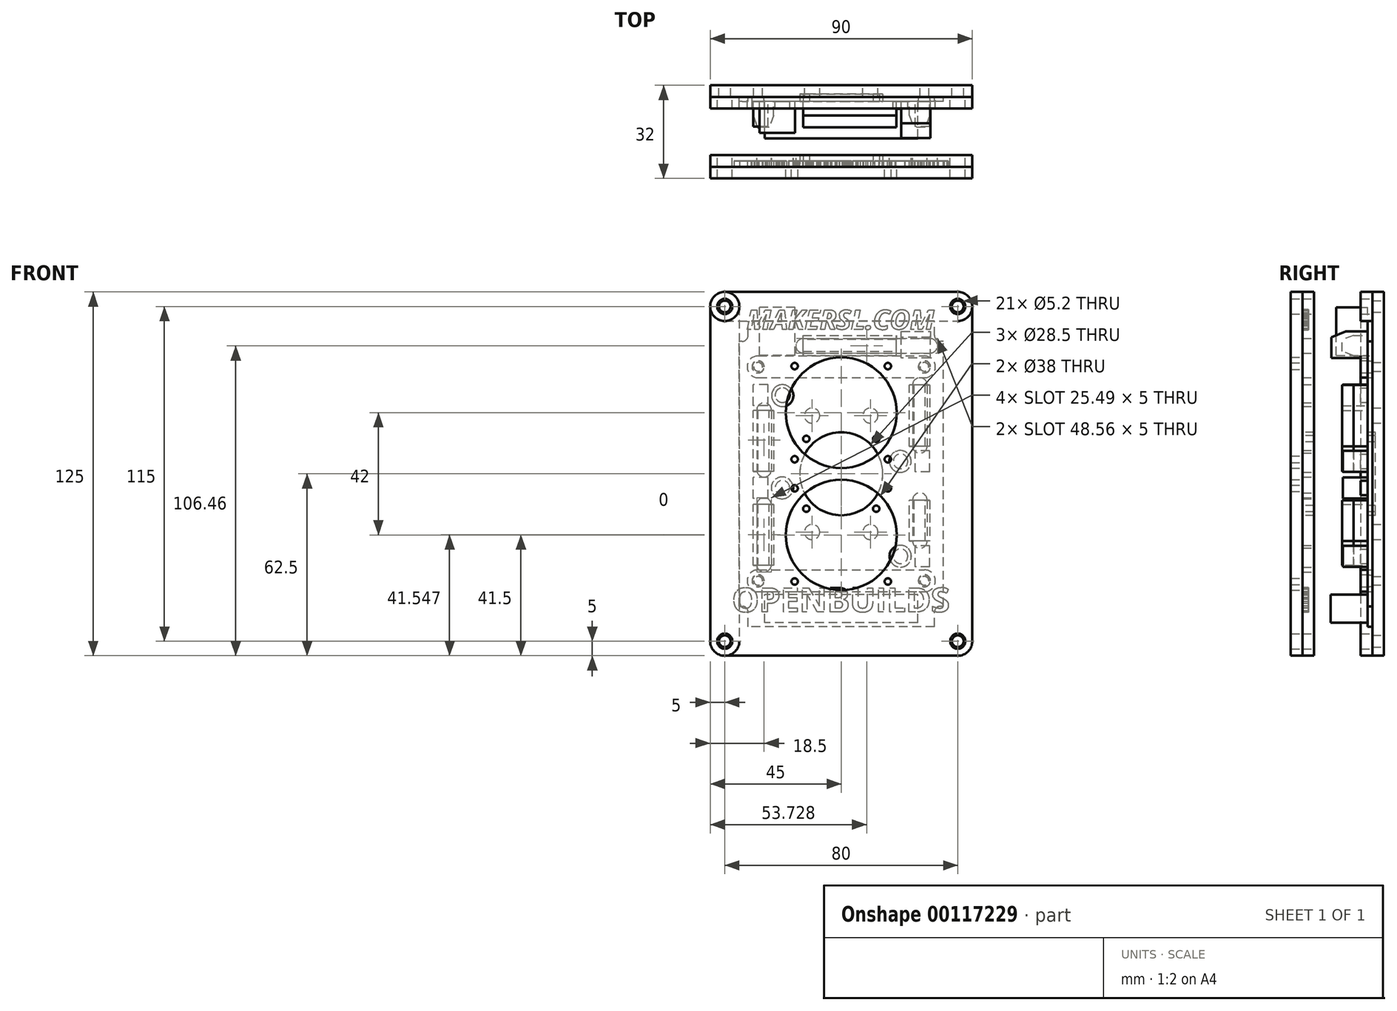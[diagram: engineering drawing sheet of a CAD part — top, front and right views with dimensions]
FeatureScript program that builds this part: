
annotation { "Feature Type Name" : "Feature", "Feature Type Description" : "" }
export const myFeature = defineFeature(function(context is Context, id is Id, definition is map)
    precondition{}
    {
        {
            var Q0;
            Q0=qCreatedBy(makeId("Front.planeOp"),FACE);
            var sketch = newSketch(context, id + "F0", { "sketchPlane" : qUnion([Q0])});
            skPoint(sketch, "E0.middle", {"position": v(0, 0) * mm});
            skLineSegment(sketch, "E1.bottom", {"start": v(10, -20) * mm, "end": v(-10, -20) * mm, "construction": true});
            skLineSegment(sketch, "E1.top", {"start": v(10, 20) * mm, "end": v(-10, 20) * mm, "construction": true});
            skLineSegment(sketch, "E1.left", {"start": v(10, -20) * mm, "end": v(10, 20) * mm, "construction": true});
            skLineSegment(sketch, "E1.right", {"start": v(-10, -20) * mm, "end": v(-10, 20) * mm, "construction": true});
            skCircle(sketch, "E2", {"center": v(-10, 20) * mm, "radius": 2.6 * mm});
            skCircle(sketch, "E3", {"center": v(10, 20) * mm, "radius": 2.6 * mm});
            skCircle(sketch, "E4", {"center": v(10, -20) * mm, "radius": 2.6 * mm});
            skCircle(sketch, "E5", {"center": v(-10, -20) * mm, "radius": 2.6 * mm});
            skLineSegment(sketch, "E6.bottom", {"start": v(28.55, -36.75) * mm, "end": v(-28.55, -36.75) * mm, "construction": true});
            skLineSegment(sketch, "E6.top", {"start": v(28.55, 36.75) * mm, "end": v(-28.55, 36.75) * mm, "construction": true});
            skLineSegment(sketch, "E6.left", {"start": v(28.55, -36.75) * mm, "end": v(28.55, 36.75) * mm, "construction": true});
            skLineSegment(sketch, "E6.right", {"start": v(-28.55, -36.75) * mm, "end": v(-28.55, 36.75) * mm, "construction": true});
            skCircle(sketch, "E7", {"center": v(-28.55, 36.75) * mm, "radius": 1.5 * mm});
            skCircle(sketch, "E8", {"center": v(28.55, 36.75) * mm, "radius": 1.5 * mm});
            skCircle(sketch, "E9", {"center": v(28.55, -36.75) * mm, "radius": 1.5 * mm});
            skCircle(sketch, "E10", {"center": v(-28.55, -36.75) * mm, "radius": 1.5 * mm});
            skLineSegment(sketch, "E11.bottom", {"start": v(40, -62.5) * mm, "end": v(-40, -62.5) * mm});
            skLineSegment(sketch, "E11.top", {"start": v(40, 62.5) * mm, "end": v(-40, 62.5) * mm});
            skLineSegment(sketch, "E11.left", {"start": v(45, -57.5) * mm, "end": v(45, 57.5) * mm});
            skLineSegment(sketch, "E11.right", {"start": v(-45, -57.5) * mm, "end": v(-45, 57.5) * mm});
            skPoint(sketch, "E12.visualSharp", {"position": v(-45, 62.5) * mm});
            skArc(sketch, "E12.filletArc", {"start": v(-40, 62.5) * mm, "mid": v(-43.54, 61.04) * mm, "end": v(-45, 57.5) * mm});
            skPoint(sketch, "E13.visualSharp", {"position": v(45, 62.5) * mm});
            skArc(sketch, "E13.filletArc", {"start": v(45, 57.5) * mm, "mid": v(43.54, 61.04) * mm, "end": v(40, 62.5) * mm});
            skPoint(sketch, "E14.visualSharp", {"position": v(45, -62.5) * mm});
            skArc(sketch, "E14.filletArc", {"start": v(40, -62.5) * mm, "mid": v(43.54, -61.04) * mm, "end": v(45, -57.5) * mm});
            skPoint(sketch, "E15.visualSharp", {"position": v(-45, -62.5) * mm});
            skArc(sketch, "E15.filletArc", {"start": v(-45, -57.5) * mm, "mid": v(-43.54, -61.04) * mm, "end": v(-40, -62.5) * mm});
            skCircle(sketch, "E16", {"center": v(-40, 57.5) * mm, "radius": 2 * mm});
            skCircle(sketch, "E17", {"center": v(40, 57.5) * mm, "radius": 2 * mm});
            skCircle(sketch, "E18", {"center": v(-40, -57.5) * mm, "radius": 2 * mm});
            skCircle(sketch, "E19", {"center": v(40, -57.5) * mm, "radius": 2 * mm});
            skSolve(sketch);
        }
        {
            var Q0;
            Q0 = qSketchRegion(id + "F0", true);
            extrude(context, id + "F1", {"entities" : qUnion([Q0]), "depth" : 4 * mm});
        }
        {
            var Q0;
            Q0=makeQuery(id+"F1.opExtrude","CAP_FACE",FACE,{"disambiguationData":[OSD([sQuery(id+"F0.wireOp",EDGE,"E2"),sQuery(id+"F0.wireOp",EDGE,"E3"),sQuery(id+"F0.wireOp",EDGE,"E4"),sQuery(id+"F0.wireOp",EDGE,"E5"),sQuery(id+"F0.wireOp",EDGE,"E7"),sQuery(id+"F0.wireOp",EDGE,"E8"),sQuery(id+"F0.wireOp",EDGE,"E9"),sQuery(id+"F0.wireOp",EDGE,"E10"),sQuery(id+"F0.wireOp",EDGE,"E11.bottom"),sQuery(id+"F0.wireOp",EDGE,"E11.top"),sQuery(id+"F0.wireOp",EDGE,"E11.left"),sQuery(id+"F0.wireOp",EDGE,"E11.right"),sQuery(id+"F0.wireOp",EDGE,"E12.filletArc"),sQuery(id+"F0.wireOp",EDGE,"E13.filletArc"),sQuery(id+"F0.wireOp",EDGE,"E14.filletArc"),sQuery(id+"F0.wireOp",EDGE,"E15.filletArc"),sQuery(id+"F0.wireOp",EDGE,"E16"),sQuery(id+"F0.wireOp",EDGE,"E17"),sQuery(id+"F0.wireOp",EDGE,"E18"),sQuery(id+"F0.wireOp",EDGE,"E19")])],"isStart":false});
            var sketch = newSketch(context, id + "F2", { "sketchPlane" : qUnion([Q0])});
            skCircle(sketch, "E20", {"center": v(-28.55, 36.75) * mm, "radius": 2.1 * mm});
            skCircle(sketch, "E21", {"center": v(28.55, 36.75) * mm, "radius": 2.1 * mm});
            skCircle(sketch, "E22", {"center": v(-28.55, -36.75) * mm, "radius": 2.1 * mm});
            skCircle(sketch, "E23", {"center": v(28.55, -36.75) * mm, "radius": 2.1 * mm});
            skLineSegment(sketch, "E24", {"start": v(-28.55, -36.75) * mm, "end": v(28.55, -36.75) * mm});
            skLineSegment(sketch, "E25", {"start": v(-28.55, 36.75) * mm, "end": v(28.55, 36.75) * mm});
            skArc(sketch, "E26.0.startCap", {"start": v(-28.55, 33) * mm, "mid": v(-32.3, 36.75) * mm, "end": v(-28.55, 40.5) * mm});
            skArc(sketch, "E26.0.endCap", {"start": v(28.55, 40.5) * mm, "mid": v(32.3, 36.75) * mm, "end": v(28.55, 33) * mm});
            skLineSegment(sketch, "E26.0.left", {"start": v(-28.55, 40.5) * mm, "end": v(28.55, 40.5) * mm});
            skLineSegment(sketch, "E26.0.right", {"start": v(-28.55, 33) * mm, "end": v(28.55, 33) * mm});
            skArc(sketch, "E27.0.startCap", {"start": v(-28.55, -40.5) * mm, "mid": v(-32.3, -36.75) * mm, "end": v(-28.55, -33) * mm});
            skArc(sketch, "E27.0.endCap", {"start": v(28.55, -33) * mm, "mid": v(32.3, -36.75) * mm, "end": v(28.55, -40.5) * mm});
            skLineSegment(sketch, "E27.0.left", {"start": v(-28.55, -33) * mm, "end": v(28.55, -33) * mm});
            skLineSegment(sketch, "E27.0.right", {"start": v(-28.55, -40.5) * mm, "end": v(28.55, -40.5) * mm});
            skSolve(sketch);
        }
        {
            var Q0;
            Q0=makeQuery(id+"F2.imprint","IMPRINT",FACE,{"disambiguationData":[TD([[makeQuery(id+"F2.imprint","IMPRINT",EDGE,{"derivedFrom":sQuery(id+"F2.wireOp",EDGE,"E20")}),-1.0]])]});
            var Q1;
            Q1=makeQuery(id+"F2.imprint","IMPRINT",FACE,{"disambiguationData":[TD([[makeQuery(id+"F2.imprint","IMPRINT",EDGE,{"derivedFrom":sQuery(id+"F2.wireOp",EDGE,"E22")}),-1.0]])]});
            extrude(context, id + "F3", {"entities" : qUnion([Q0, Q1]), "depth" : 4 * mm});
        }
        {
            var Q0;
            Q0=makeQuery(id+"F1.opExtrude","CAP_FACE",FACE,{"disambiguationData":[OSD([sQuery(id+"F0.wireOp",EDGE,"E2"),sQuery(id+"F0.wireOp",EDGE,"E3"),sQuery(id+"F0.wireOp",EDGE,"E4"),sQuery(id+"F0.wireOp",EDGE,"E5"),sQuery(id+"F0.wireOp",EDGE,"E7"),sQuery(id+"F0.wireOp",EDGE,"E8"),sQuery(id+"F0.wireOp",EDGE,"E9"),sQuery(id+"F0.wireOp",EDGE,"E10"),sQuery(id+"F0.wireOp",EDGE,"E11.bottom"),sQuery(id+"F0.wireOp",EDGE,"E11.top"),sQuery(id+"F0.wireOp",EDGE,"E11.left"),sQuery(id+"F0.wireOp",EDGE,"E11.right"),sQuery(id+"F0.wireOp",EDGE,"E12.filletArc"),sQuery(id+"F0.wireOp",EDGE,"E13.filletArc"),sQuery(id+"F0.wireOp",EDGE,"E14.filletArc"),sQuery(id+"F0.wireOp",EDGE,"E15.filletArc"),sQuery(id+"F0.wireOp",EDGE,"E16"),sQuery(id+"F0.wireOp",EDGE,"E17"),sQuery(id+"F0.wireOp",EDGE,"E18"),sQuery(id+"F0.wireOp",EDGE,"E19")])],"isStart":false});
            var sketch = newSketch(context, id + "F4", { "sketchPlane" : qUnion([Q0])});
            skCircle(sketch, "E28", {"center": v(-40, 57.5) * mm, "radius": 2.6 * mm});
            skCircle(sketch, "E29", {"center": v(40, 57.5) * mm, "radius": 2.6 * mm});
            skLineSegment(sketch, "E30", {"start": v(-40, 57.5) * mm, "end": v(40, 57.5) * mm});
            skArc(sketch, "E31.0.startCap", {"start": v(-40, 52.5) * mm, "mid": v(-45, 57.5) * mm, "end": v(-40, 62.5) * mm});
            skArc(sketch, "E31.0.endCap", {"start": v(40, 62.5) * mm, "mid": v(45, 57.5) * mm, "end": v(40, 52.5) * mm});
            skLineSegment(sketch, "E31.0.left", {"start": v(-40, 62.5) * mm, "end": v(40, 62.5) * mm});
            skLineSegment(sketch, "E31.0.right", {"start": v(-40, 52.5) * mm, "end": v(40, 52.5) * mm});
            skSolve(sketch);
        }
        {
            var Q0;
            Q0=makeQuery(id+"F4.imprint","IMPRINT",FACE,{"disambiguationData":[TD([[makeQuery(id+"F4.imprint","IMPRINT",EDGE,{"derivedFrom":sQuery(id+"F4.wireOp",EDGE,"E28")}),-1.0]])]});
            extrude(context, id + "F5", {"entities" : qUnion([Q0]), "depth" : 4 * mm});
        }
        {
            var Q0;
            Q0=makeQuery(id+"F1.opExtrude","CAP_FACE",FACE,{"disambiguationData":[OSD([sQuery(id+"F0.wireOp",EDGE,"E2"),sQuery(id+"F0.wireOp",EDGE,"E3"),sQuery(id+"F0.wireOp",EDGE,"E4"),sQuery(id+"F0.wireOp",EDGE,"E5"),sQuery(id+"F0.wireOp",EDGE,"E7"),sQuery(id+"F0.wireOp",EDGE,"E8"),sQuery(id+"F0.wireOp",EDGE,"E9"),sQuery(id+"F0.wireOp",EDGE,"E10"),sQuery(id+"F0.wireOp",EDGE,"E11.bottom"),sQuery(id+"F0.wireOp",EDGE,"E11.top"),sQuery(id+"F0.wireOp",EDGE,"E11.left"),sQuery(id+"F0.wireOp",EDGE,"E11.right"),sQuery(id+"F0.wireOp",EDGE,"E12.filletArc"),sQuery(id+"F0.wireOp",EDGE,"E13.filletArc"),sQuery(id+"F0.wireOp",EDGE,"E14.filletArc"),sQuery(id+"F0.wireOp",EDGE,"E15.filletArc"),sQuery(id+"F0.wireOp",EDGE,"E16"),sQuery(id+"F0.wireOp",EDGE,"E17"),sQuery(id+"F0.wireOp",EDGE,"E18"),sQuery(id+"F0.wireOp",EDGE,"E19")])],"isStart":false});
            var sketch = newSketch(context, id + "F6", { "sketchPlane" : qUnion([Q0])});
            skCircle(sketch, "E32", {"center": v(-40, -57.5) * mm, "radius": 2.6 * mm});
            skCircle(sketch, "E33", {"center": v(-40, 57.5) * mm, "radius": 2.6 * mm});
            skLineSegment(sketch, "E34", {"start": v(-40, 57.5) * mm, "end": v(-40, -57.5) * mm});
            skArc(sketch, "E35.0.startCap", {"start": v(-45, 57.5) * mm, "mid": v(-40, 62.5) * mm, "end": v(-35, 57.5) * mm});
            skArc(sketch, "E35.0.endCap", {"start": v(-35, -57.5) * mm, "mid": v(-40, -62.5) * mm, "end": v(-45, -57.5) * mm});
            skLineSegment(sketch, "E35.0.left", {"start": v(-35, 57.5) * mm, "end": v(-35, -57.5) * mm});
            skLineSegment(sketch, "E35.0.right", {"start": v(-45, 57.5) * mm, "end": v(-45, -57.5) * mm});
            skSolve(sketch);
        }
        {
            var Q0;
            Q0=makeQuery(id+"F6.imprint","IMPRINT",FACE,{"disambiguationData":[TD([[makeQuery(id+"F6.imprint","IMPRINT",EDGE,{"derivedFrom":sQuery(id+"F6.wireOp",EDGE,"E32")}),-1.0]])]});
            extrude(context, id + "F7", {"entities" : qUnion([Q0]), "depth" : 4 * mm});
        }
        {
            var Q0;
            Q0=makeQuery(id+"F1.opExtrude","CAP_FACE",FACE,{"disambiguationData":[OSD([sQuery(id+"F0.wireOp",EDGE,"E2"),sQuery(id+"F0.wireOp",EDGE,"E3"),sQuery(id+"F0.wireOp",EDGE,"E4"),sQuery(id+"F0.wireOp",EDGE,"E5"),sQuery(id+"F0.wireOp",EDGE,"E7"),sQuery(id+"F0.wireOp",EDGE,"E8"),sQuery(id+"F0.wireOp",EDGE,"E9"),sQuery(id+"F0.wireOp",EDGE,"E10"),sQuery(id+"F0.wireOp",EDGE,"E11.bottom"),sQuery(id+"F0.wireOp",EDGE,"E11.top"),sQuery(id+"F0.wireOp",EDGE,"E11.left"),sQuery(id+"F0.wireOp",EDGE,"E11.right"),sQuery(id+"F0.wireOp",EDGE,"E12.filletArc"),sQuery(id+"F0.wireOp",EDGE,"E13.filletArc"),sQuery(id+"F0.wireOp",EDGE,"E14.filletArc"),sQuery(id+"F0.wireOp",EDGE,"E15.filletArc"),sQuery(id+"F0.wireOp",EDGE,"E16"),sQuery(id+"F0.wireOp",EDGE,"E17"),sQuery(id+"F0.wireOp",EDGE,"E18"),sQuery(id+"F0.wireOp",EDGE,"E19")])],"isStart":false});
            var sketch = newSketch(context, id + "F8", { "sketchPlane" : qUnion([Q0])});
            skLineSegment(sketch, "E36.bottom", {"start": v(32, -52.5) * mm, "end": v(-32, -52.5) * mm});
            skLineSegment(sketch, "E36.top", {"start": v(32, 52.5) * mm, "end": v(-32, 52.5) * mm});
            skLineSegment(sketch, "E36.left", {"start": v(35, -45.5) * mm, "end": v(35, 45.5) * mm});
            skLineSegment(sketch, "E36.right", {"start": v(-35, -45.5) * mm, "end": v(-35, 45.5) * mm});
            skPoint(sketch, "E36.middle", {"position": v(0, 0) * mm});
            skLineSegment(sketch, "E37.bottom", {"start": v(-34, 45.5) * mm, "end": v(-35, 45.5) * mm});
            skLineSegment(sketch, "E37.left", {"start": v(-32, 47.5) * mm, "end": v(-32, 52.5) * mm});
            skPoint(sketch, "E37.middle", {"position": v(-35, 52.5) * mm});
            skLineSegment(sketch, "E38.bottom", {"start": v(35, 45.5) * mm, "end": v(34, 45.5) * mm});
            skLineSegment(sketch, "E38.right", {"start": v(32, 47.5) * mm, "end": v(32, 52.5) * mm});
            skPoint(sketch, "E38.middle", {"position": v(35, 52.5) * mm});
            skLineSegment(sketch, "E39.top", {"start": v(35, -45.5) * mm, "end": v(34, -45.5) * mm});
            skLineSegment(sketch, "E39.right", {"start": v(32, -52.5) * mm, "end": v(32, -47.5) * mm});
            skPoint(sketch, "E39.middle", {"position": v(35, -52.5) * mm});
            skLineSegment(sketch, "E40.top", {"start": v(-35, -45.5) * mm, "end": v(-34, -45.5) * mm});
            skLineSegment(sketch, "E40.right", {"start": v(-32, -52.5) * mm, "end": v(-32, -47.5) * mm});
            skPoint(sketch, "E40.middle", {"position": v(-35, -52.5) * mm});
            skPoint(sketch, "E40.left.end.orphan", {"position": v(-38, -45.5) * mm});
            skPoint(sketch, "E40.bottom.start.orphan", {"position": v(-38, -59.5) * mm});
            skPoint(sketch, "E41.orphan", {"position": v(-32, -59.5) * mm});
            skPoint(sketch, "E42.visualSharp", {"position": v(-32, -45.5) * mm});
            skArc(sketch, "E42.filletArc", {"start": v(-32, -47.5) * mm, "mid": v(-32.59, -46.09) * mm, "end": v(-34, -45.5) * mm});
            skPoint(sketch, "E43.visualSharp", {"position": v(32, -45.5) * mm});
            skArc(sketch, "E43.filletArc", {"start": v(34, -45.5) * mm, "mid": v(32.59, -46.09) * mm, "end": v(32, -47.5) * mm});
            skPoint(sketch, "E44.visualSharp", {"position": v(32, 45.5) * mm});
            skArc(sketch, "E44.filletArc", {"start": v(32, 47.5) * mm, "mid": v(32.59, 46.09) * mm, "end": v(34, 45.5) * mm});
            skPoint(sketch, "E45.visualSharp", {"position": v(-32, 45.5) * mm});
            skArc(sketch, "E45.filletArc", {"start": v(-34, 45.5) * mm, "mid": v(-32.59, 46.09) * mm, "end": v(-32, 47.5) * mm});
            skPoint(sketch, "E37.right.end.orphan", {"position": v(-38, 59.5) * mm});
            skPoint(sketch, "E46.orphan", {"position": v(-38, 45.5) * mm});
            skPoint(sketch, "E47.orphan", {"position": v(-32, 59.5) * mm});
            skPoint(sketch, "E38.left.start.orphan", {"position": v(38, 45.5) * mm});
            skPoint(sketch, "E38.top.end.orphan", {"position": v(32, 59.5) * mm});
            skPoint(sketch, "E38.top.start.orphan", {"position": v(38, 59.5) * mm});
            skPoint(sketch, "E39.bottom.end.orphan", {"position": v(32, -59.5) * mm});
            skPoint(sketch, "E39.left.end.orphan", {"position": v(38, -45.5) * mm});
            skPoint(sketch, "E39.left.start.orphan", {"position": v(38, -59.5) * mm});
            skCircle(sketch, "E48", {"center": v(-28.55, 36.75) * mm, "radius": 2 * mm});
            skCircle(sketch, "E49", {"center": v(28.55, 36.75) * mm, "radius": 2 * mm});
            skCircle(sketch, "E50", {"center": v(28.55, -36.75) * mm, "radius": 2 * mm});
            skCircle(sketch, "E51", {"center": v(-28.55, -36.75) * mm, "radius": 2 * mm});
            skSolve(sketch);
        }
        {
            var Q0;
            Q0 = qSketchRegion(id + "F8", true);
            extrude(context, id + "F9", {"entities" : qUnion([Q0]), "depth" : 1.6 * mm});
        }
        {
            var Q0;
            Q0=makeQuery(id+"F9.opExtrude","CAP_FACE",FACE,{"disambiguationData":[OSD([sQuery(id+"F8.wireOp",EDGE,"E36.bottom"),sQuery(id+"F8.wireOp",EDGE,"E36.top"),sQuery(id+"F8.wireOp",EDGE,"E36.left"),sQuery(id+"F8.wireOp",EDGE,"E36.right"),sQuery(id+"F8.wireOp",EDGE,"E37.bottom"),sQuery(id+"F8.wireOp",EDGE,"E37.left"),sQuery(id+"F8.wireOp",EDGE,"E38.bottom"),sQuery(id+"F8.wireOp",EDGE,"E38.right"),sQuery(id+"F8.wireOp",EDGE,"E39.top"),sQuery(id+"F8.wireOp",EDGE,"E39.right"),sQuery(id+"F8.wireOp",EDGE,"E40.top"),sQuery(id+"F8.wireOp",EDGE,"E40.right"),sQuery(id+"F8.wireOp",EDGE,"E42.filletArc"),sQuery(id+"F8.wireOp",EDGE,"E43.filletArc"),sQuery(id+"F8.wireOp",EDGE,"E44.filletArc"),sQuery(id+"F8.wireOp",EDGE,"E45.filletArc"),sQuery(id+"F8.wireOp",EDGE,"E48"),sQuery(id+"F8.wireOp",EDGE,"E49"),sQuery(id+"F8.wireOp",EDGE,"E50"),sQuery(id+"F8.wireOp",EDGE,"E51")])],"isStart":false});
            var sketch = newSketch(context, id + "F10", { "sketchPlane" : qUnion([Q0])});
            skLineSegment(sketch, "E52.bottom", {"start": v(-15.9, 40.7) * mm, "end": v(-28.1, 40.7) * mm});
            skLineSegment(sketch, "E52.top", {"start": v(-15.9, 57.2) * mm, "end": v(-28.1, 57.2) * mm});
            skLineSegment(sketch, "E52.left", {"start": v(-15.9, 40.7) * mm, "end": v(-15.9, 57.2) * mm});
            skLineSegment(sketch, "E52.right", {"start": v(-28.1, 40.7) * mm, "end": v(-28.1, 57.2) * mm});
            skPoint(sketch, "E52.middle", {"position": v(-22, 48.95) * mm});
            skLineSegment(sketch, "E53.bottom", {"start": v(30.6, 39.8) * mm, "end": v(20.6, 39.8) * mm});
            skLineSegment(sketch, "E53.top", {"start": v(30.6, 48.9) * mm, "end": v(20.6, 48.9) * mm});
            skLineSegment(sketch, "E53.left", {"start": v(30.6, 39.8) * mm, "end": v(30.6, 48.9) * mm});
            skLineSegment(sketch, "E53.right", {"start": v(20.6, 39.8) * mm, "end": v(20.6, 48.9) * mm});
            skPoint(sketch, "E53.middle", {"position": v(25.6, 44.35) * mm});
            skLineSegment(sketch, "E54.bottom", {"start": v(18.9, 40.6) * mm, "end": v(-13.1, 40.6) * mm});
            skLineSegment(sketch, "E54.top", {"start": v(18.9, 47.6) * mm, "end": v(-13.1, 47.6) * mm});
            skLineSegment(sketch, "E54.left", {"start": v(18.9, 40.6) * mm, "end": v(18.9, 47.6) * mm});
            skLineSegment(sketch, "E54.right", {"start": v(-13.1, 40.6) * mm, "end": v(-13.1, 47.6) * mm});
            skPoint(sketch, "E54.middle", {"position": v(2.9, 44.1) * mm});
            skLineSegment(sketch, "E55.bottom", {"start": v(30.35, 9.5) * mm, "end": v(23.35, 9.5) * mm});
            skLineSegment(sketch, "E55.top", {"start": v(30.35, 30.5) * mm, "end": v(23.35, 30.5) * mm});
            skLineSegment(sketch, "E55.left", {"start": v(30.35, 9.5) * mm, "end": v(30.35, 30.5) * mm});
            skLineSegment(sketch, "E55.right", {"start": v(23.35, 9.5) * mm, "end": v(23.35, 30.5) * mm});
            skPoint(sketch, "E55.middle", {"position": v(26.85, 20) * mm});
            skLineSegment(sketch, "E56.bottom", {"start": v(-23.2, -31.5) * mm, "end": v(-30.2, -31.5) * mm});
            skLineSegment(sketch, "E56.top", {"start": v(-23.2, -10.5) * mm, "end": v(-30.2, -10.5) * mm});
            skLineSegment(sketch, "E56.left", {"start": v(-23.2, -31.5) * mm, "end": v(-23.2, -10.5) * mm});
            skLineSegment(sketch, "E56.right", {"start": v(-30.2, -31.5) * mm, "end": v(-30.2, -10.5) * mm});
            skPoint(sketch, "E56.middle", {"position": v(-26.7, -21) * mm});
            skLineSegment(sketch, "E57.bottom", {"start": v(-23.2, 0.8) * mm, "end": v(-30.2, 0.8) * mm});
            skLineSegment(sketch, "E57.top", {"start": v(-23.2, 21.8) * mm, "end": v(-30.2, 21.8) * mm});
            skLineSegment(sketch, "E57.left", {"start": v(-23.2, 0.8) * mm, "end": v(-23.2, 21.8) * mm});
            skLineSegment(sketch, "E57.right", {"start": v(-30.2, 0.8) * mm, "end": v(-30.2, 21.8) * mm});
            skPoint(sketch, "E57.middle", {"position": v(-26.7, 11.3) * mm});
            skLineSegment(sketch, "E58.bottom", {"start": v(26.25, -51.1) * mm, "end": v(-26.25, -51.1) * mm});
            skLineSegment(sketch, "E58.top", {"start": v(26.25, -41.5) * mm, "end": v(-26.25, -41.5) * mm});
            skLineSegment(sketch, "E58.left", {"start": v(26.25, -51.1) * mm, "end": v(26.25, -41.5) * mm});
            skLineSegment(sketch, "E58.right", {"start": v(-26.25, -51.1) * mm, "end": v(-26.25, -41.5) * mm});
            skPoint(sketch, "E58.middle", {"position": v(0, -46.3) * mm});
            skLineSegment(sketch, "E59.bottom", {"start": v(30.35, -23.1) * mm, "end": v(23.35, -23.1) * mm});
            skLineSegment(sketch, "E59.top", {"start": v(30.35, -9.1) * mm, "end": v(23.35, -9.1) * mm});
            skLineSegment(sketch, "E59.left", {"start": v(30.35, -23.1) * mm, "end": v(30.35, -9.1) * mm});
            skLineSegment(sketch, "E59.right", {"start": v(23.35, -23.1) * mm, "end": v(23.35, -9.1) * mm});
            skPoint(sketch, "E59.middle", {"position": v(26.85, -16.1) * mm});
            skLineSegment(sketch, "E60.bottom", {"start": v(30.35, -31.95) * mm, "end": v(25.35, -31.95) * mm});
            skLineSegment(sketch, "E60.top", {"start": v(30.35, -24.7) * mm, "end": v(25.35, -24.7) * mm});
            skLineSegment(sketch, "E60.left", {"start": v(30.35, -31.95) * mm, "end": v(30.35, -24.7) * mm});
            skLineSegment(sketch, "E60.right", {"start": v(25.35, -31.95) * mm, "end": v(25.35, -24.7) * mm});
            skPoint(sketch, "E60.middle", {"position": v(27.85, -28.33) * mm});
            skLineSegment(sketch, "E61.bottom", {"start": v(30.35, 0.65) * mm, "end": v(25.35, 0.65) * mm});
            skLineSegment(sketch, "E61.top", {"start": v(30.35, 7.9) * mm, "end": v(25.35, 7.9) * mm});
            skLineSegment(sketch, "E61.left", {"start": v(30.35, 0.65) * mm, "end": v(30.35, 7.9) * mm});
            skLineSegment(sketch, "E61.right", {"start": v(25.35, 0.65) * mm, "end": v(25.35, 7.9) * mm});
            skPoint(sketch, "E61.middle", {"position": v(27.85, 4.28) * mm});
            skLineSegment(sketch, "E62.bottom", {"start": v(-25.2, 23.4) * mm, "end": v(-30.2, 23.4) * mm});
            skLineSegment(sketch, "E62.top", {"start": v(-25.2, 30.65) * mm, "end": v(-30.2, 30.65) * mm});
            skLineSegment(sketch, "E62.left", {"start": v(-25.2, 23.4) * mm, "end": v(-25.2, 30.65) * mm});
            skLineSegment(sketch, "E62.right", {"start": v(-30.2, 23.4) * mm, "end": v(-30.2, 30.65) * mm});
            skPoint(sketch, "E62.middle", {"position": v(-27.7, 27.02) * mm});
            skLineSegment(sketch, "E63.bottom", {"start": v(-25.2, -8.45) * mm, "end": v(-30.2, -8.45) * mm});
            skLineSegment(sketch, "E63.top", {"start": v(-25.2, -1.2) * mm, "end": v(-30.2, -1.2) * mm});
            skLineSegment(sketch, "E63.left", {"start": v(-25.2, -8.45) * mm, "end": v(-25.2, -1.2) * mm});
            skLineSegment(sketch, "E63.right", {"start": v(-30.2, -8.45) * mm, "end": v(-30.2, -1.2) * mm});
            skPoint(sketch, "E63.middle", {"position": v(-27.7, -4.83) * mm});
            skCircle(sketch, "E64", {"center": v(-20.2, 27.02) * mm, "radius": 2.5 * mm});
            skCircle(sketch, "E65", {"center": v(20.35, 4.28) * mm, "radius": 2.5 * mm});
            skCircle(sketch, "E66", {"center": v(20.35, -28.33) * mm, "radius": 2.5 * mm});
            skCircle(sketch, "E67", {"center": v(-20.2, -4.83) * mm, "radius": 2.5 * mm});
            skPoint(sketch, "E67.centerSnap0", {"position": v(-25.2, -4.83) * mm});
            skSolve(sketch);
        }
        {
            var Q0;
            {var subQ0=sQuery(id+"F10.wireOp",EDGE,"E52.top");Q0=makeQuery(id+"F10.imprint","IMPRINT",FACE,{"disambiguationData":[TD([[makeQuery(id+"F10.imprint","IMPRINT",EDGE,{"derivedFrom":subQ0}),1.0]])]});}
            var Q1;
            {var subQ0=sQuery(id+"F10.wireOp",EDGE,"E52.bottom");Q1=makeQuery(id+"F10.imprint","IMPRINT",FACE,{"disambiguationData":[TD([[makeQuery(id+"F10.imprint","IMPRINT",EDGE,{"derivedFrom":subQ0}),-1.0]])]});}
            extrude(context, id + "F11", {"entities" : qUnion([Q0, Q1]), "depth" : 10.8 * mm});
        }
        {
            var Q0;
            Q0=makeQuery(id+"F10.imprint","IMPRINT",FACE,{"disambiguationData":[TD([[makeQuery(id+"F10.imprint","IMPRINT",EDGE,{"derivedFrom":sQuery(id+"F10.wireOp",EDGE,"E53.bottom")}),-1.0]])]});
            extrude(context, id + "F12", {"entities" : qUnion([Q0]), "depth" : 12.5 * mm});
        }
        {
            var Q0;
            Q0=makeQuery(id+"F10.imprint","IMPRINT",FACE,{"disambiguationData":[TD([[makeQuery(id+"F10.imprint","IMPRINT",EDGE,{"derivedFrom":sQuery(id+"F10.wireOp",EDGE,"E54.bottom")}),-1.0]])]});
            extrude(context, id + "F13", {"entities" : qUnion([Q0]), "depth" : 8.85 * mm});
        }
        {
            var Q0;
            Q0=makeQuery(id+"F13.opExtrude","CAP_EDGE",EDGE,{"disambiguationData":[OSD([sQuery(id+"F10.wireOp",EDGE,"E54.top")])],"isStart":false});
            var Q1;
            Q1=makeQuery(id+"F13.opExtrude","CAP_EDGE",EDGE,{"disambiguationData":[OSD([sQuery(id+"F10.wireOp",EDGE,"E54.bottom")])],"isStart":false});
            chamfer(context, id + "F14", {"entities" : qUnion([Q0, Q1]), "chamferType" : ChamferType.TWO_OFFSETS, "width1" : 1.5 * mm, "oppositeDirection" : false, "width2" : 4 * mm, "tangentPropagation" : true});
        }
        {
            var Q0;
            Q0=makeQuery(id+"F12.opExtrude","CAP_EDGE",EDGE,{"disambiguationData":[OSD([sQuery(id+"F10.wireOp",EDGE,"E53.top")])],"isStart":false});
            chamfer(context, id + "F15", {"entities" : qUnion([Q0]), "chamferType" : ChamferType.TWO_OFFSETS, "width1" : 2 * mm, "oppositeDirection" : false, "width2" : 5 * mm, "tangentPropagation" : true});
        }
        {
            var Q0;
            Q0=makeQuery(id+"F10.imprint","IMPRINT",FACE,{"disambiguationData":[TD([[makeQuery(id+"F10.imprint","IMPRINT",EDGE,{"derivedFrom":sQuery(id+"F10.wireOp",EDGE,"E55.bottom")}),-1.0]])]});
            var Q1;
            Q1=makeQuery(id+"F10.imprint","IMPRINT",FACE,{"disambiguationData":[TD([[makeQuery(id+"F10.imprint","IMPRINT",EDGE,{"derivedFrom":sQuery(id+"F10.wireOp",EDGE,"E57.bottom")}),-1.0]])]});
            var Q2;
            Q2=makeQuery(id+"F10.imprint","IMPRINT",FACE,{"disambiguationData":[TD([[makeQuery(id+"F10.imprint","IMPRINT",EDGE,{"derivedFrom":sQuery(id+"F10.wireOp",EDGE,"E56.bottom")}),-1.0]])]});
            extrude(context, id + "F16", {"entities" : qUnion([Q0, Q1, Q2]), "depth" : 8.8 * mm});
        }
        {
            var Q0;
            Q0=makeQuery(id+"F10.imprint","IMPRINT",FACE,{"disambiguationData":[TD([[makeQuery(id+"F10.imprint","IMPRINT",EDGE,{"derivedFrom":sQuery(id+"F10.wireOp",EDGE,"E58.bottom")}),-1.0]])]});
            extrude(context, id + "F17", {"entities" : qUnion([Q0]), "depth" : 12.7 * mm});
        }
        {
            var Q0;
            Q0=makeQuery(id+"F10.imprint","IMPRINT",FACE,{"disambiguationData":[TD([[makeQuery(id+"F10.imprint","IMPRINT",EDGE,{"derivedFrom":sQuery(id+"F10.wireOp",EDGE,"E59.bottom")}),-1.0]])]});
            extrude(context, id + "F18", {"entities" : qUnion([Q0]), "depth" : 8.8 * mm});
        }
        {
            var Q0;
            Q0=makeQuery(id+"F18.opExtrude","CAP_EDGE",EDGE,{"disambiguationData":[OSD([sQuery(id+"F10.wireOp",EDGE,"E59.left")])],"isStart":false});
            var Q1;
            Q1=makeQuery(id+"F18.opExtrude","CAP_EDGE",EDGE,{"disambiguationData":[OSD([sQuery(id+"F10.wireOp",EDGE,"E59.right")])],"isStart":false});
            chamfer(context, id + "F19", {"entities" : qUnion([Q0, Q1]), "chamferType" : ChamferType.TWO_OFFSETS, "width1" : 1.5 * mm, "oppositeDirection" : false, "width2" : 4 * mm, "tangentPropagation" : true});
        }
        {
            var Q0;
            Q0=makeQuery(id+"F10.imprint","IMPRINT",FACE,{"disambiguationData":[TD([[makeQuery(id+"F10.imprint","IMPRINT",EDGE,{"derivedFrom":sQuery(id+"F10.wireOp",EDGE,"E62.bottom")}),-1.0]])]});
            var Q1;
            Q1=makeQuery(id+"F10.imprint","IMPRINT",FACE,{"disambiguationData":[TD([[makeQuery(id+"F10.imprint","IMPRINT",EDGE,{"derivedFrom":sQuery(id+"F10.wireOp",EDGE,"E63.bottom")}),-1.0]])]});
            var Q2;
            Q2=makeQuery(id+"F10.imprint","IMPRINT",FACE,{"disambiguationData":[TD([[makeQuery(id+"F10.imprint","IMPRINT",EDGE,{"derivedFrom":sQuery(id+"F10.wireOp",EDGE,"E61.bottom")}),-1.0]])]});
            var Q3;
            Q3=makeQuery(id+"F10.imprint","IMPRINT",FACE,{"disambiguationData":[TD([[makeQuery(id+"F10.imprint","IMPRINT",EDGE,{"derivedFrom":sQuery(id+"F10.wireOp",EDGE,"E60.bottom")}),-1.0]])]});
            extrude(context, id + "F20", {"entities" : qUnion([Q0, Q1, Q2, Q3]), "depth" : 8.6 * mm});
        }
        {
            var Q0;
            Q0=makeQuery(id+"F16.opExtrude","CAP_EDGE",EDGE,{"disambiguationData":[OSD([sQuery(id+"F10.wireOp",EDGE,"E57.right")])],"isStart":false});
            var Q1;
            Q1=makeQuery(id+"F16.opExtrude","CAP_EDGE",EDGE,{"disambiguationData":[OSD([sQuery(id+"F10.wireOp",EDGE,"E57.left")])],"isStart":false});
            var Q2;
            Q2=makeQuery(id+"F16.opExtrude","CAP_EDGE",EDGE,{"disambiguationData":[OSD([sQuery(id+"F10.wireOp",EDGE,"E55.right")])],"isStart":false});
            var Q3;
            Q3=makeQuery(id+"F16.opExtrude","CAP_EDGE",EDGE,{"disambiguationData":[OSD([sQuery(id+"F10.wireOp",EDGE,"E55.left")])],"isStart":false});
            var Q4;
            Q4=makeQuery(id+"F16.opExtrude","CAP_EDGE",EDGE,{"disambiguationData":[OSD([sQuery(id+"F10.wireOp",EDGE,"E56.right")])],"isStart":false});
            var Q5;
            Q5=makeQuery(id+"F16.opExtrude","CAP_EDGE",EDGE,{"disambiguationData":[OSD([sQuery(id+"F10.wireOp",EDGE,"E56.left")])],"isStart":false});
            chamfer(context, id + "F21", {"entities" : qUnion([Q0, Q1, Q2, Q3, Q4, Q5]), "chamferType" : ChamferType.TWO_OFFSETS, "width1" : 4 * mm, "oppositeDirection" : false, "width2" : 1.5 * mm, "tangentPropagation" : true});
        }
        {
            var Q0;
            Q0=makeQuery(id+"F10.imprint","IMPRINT",FACE,{"disambiguationData":[TD([[makeQuery(id+"F10.imprint","IMPRINT",EDGE,{"derivedFrom":sQuery(id+"F10.wireOp",EDGE,"E64")}),1.0]])]});
            var Q1;
            Q1=makeQuery(id+"F10.imprint","IMPRINT",FACE,{"disambiguationData":[TD([[makeQuery(id+"F10.imprint","IMPRINT",EDGE,{"derivedFrom":sQuery(id+"F10.wireOp",EDGE,"E65")}),1.0]])]});
            var Q2;
            Q2=makeQuery(id+"F10.imprint","IMPRINT",FACE,{"disambiguationData":[TD([[makeQuery(id+"F10.imprint","IMPRINT",EDGE,{"derivedFrom":sQuery(id+"F10.wireOp",EDGE,"E67")}),1.0]])]});
            var Q3;
            Q3=makeQuery(id+"F10.imprint","IMPRINT",FACE,{"disambiguationData":[TD([[makeQuery(id+"F10.imprint","IMPRINT",EDGE,{"derivedFrom":sQuery(id+"F10.wireOp",EDGE,"E66")}),1.0]])]});
            extrude(context, id + "F22", {"entities" : qUnion([Q0, Q1, Q2, Q3]), "depth" : 2.5 * mm});
        }
        {
            var Q0;
            Q0=makeQuery(id+"F1.opExtrude","CAP_FACE",FACE,{"disambiguationData":[OSD([sQuery(id+"F0.wireOp",EDGE,"E2"),sQuery(id+"F0.wireOp",EDGE,"E3"),sQuery(id+"F0.wireOp",EDGE,"E4"),sQuery(id+"F0.wireOp",EDGE,"E5"),sQuery(id+"F0.wireOp",EDGE,"E7"),sQuery(id+"F0.wireOp",EDGE,"E8"),sQuery(id+"F0.wireOp",EDGE,"E9"),sQuery(id+"F0.wireOp",EDGE,"E10"),sQuery(id+"F0.wireOp",EDGE,"E11.bottom"),sQuery(id+"F0.wireOp",EDGE,"E11.top"),sQuery(id+"F0.wireOp",EDGE,"E11.left"),sQuery(id+"F0.wireOp",EDGE,"E11.right"),sQuery(id+"F0.wireOp",EDGE,"E12.filletArc"),sQuery(id+"F0.wireOp",EDGE,"E13.filletArc"),sQuery(id+"F0.wireOp",EDGE,"E14.filletArc"),sQuery(id+"F0.wireOp",EDGE,"E15.filletArc"),sQuery(id+"F0.wireOp",EDGE,"E16"),sQuery(id+"F0.wireOp",EDGE,"E17"),sQuery(id+"F0.wireOp",EDGE,"E18"),sQuery(id+"F0.wireOp",EDGE,"E19")])],"isStart":false});
            var sketch = newSketch(context, id + "F23", { "sketchPlane" : qUnion([Q0])});
            skCircle(sketch, "E68", {"center": v(-40, 57.5) * mm, "radius": 2.6 * mm});
            skCircle(sketch, "E69", {"center": v(-40, 57.5) * mm, "radius": 5 * mm});
            skSolve(sketch);
        }
        {
            var Q0;
            Q0=makeQuery(id+"F23.imprint","IMPRINT",FACE,{"disambiguationData":[TD([[makeQuery(id+"F23.imprint","IMPRINT",EDGE,{"derivedFrom":sQuery(id+"F23.wireOp",EDGE,"E68")}),-1.0]])]});
            extrude(context, id + "F24", {"entities" : qUnion([Q0]), "depth" : 4 * mm});
        }
        {
            var Q0;
            Q0=makeQuery(id+"F1.opExtrude","CAP_FACE",FACE,{"disambiguationData":[OSD([sQuery(id+"F0.wireOp",EDGE,"E2"),sQuery(id+"F0.wireOp",EDGE,"E3"),sQuery(id+"F0.wireOp",EDGE,"E4"),sQuery(id+"F0.wireOp",EDGE,"E5"),sQuery(id+"F0.wireOp",EDGE,"E7"),sQuery(id+"F0.wireOp",EDGE,"E8"),sQuery(id+"F0.wireOp",EDGE,"E9"),sQuery(id+"F0.wireOp",EDGE,"E10"),sQuery(id+"F0.wireOp",EDGE,"E11.bottom"),sQuery(id+"F0.wireOp",EDGE,"E11.top"),sQuery(id+"F0.wireOp",EDGE,"E11.left"),sQuery(id+"F0.wireOp",EDGE,"E11.right"),sQuery(id+"F0.wireOp",EDGE,"E12.filletArc"),sQuery(id+"F0.wireOp",EDGE,"E13.filletArc"),sQuery(id+"F0.wireOp",EDGE,"E14.filletArc"),sQuery(id+"F0.wireOp",EDGE,"E15.filletArc"),sQuery(id+"F0.wireOp",EDGE,"E16"),sQuery(id+"F0.wireOp",EDGE,"E17"),sQuery(id+"F0.wireOp",EDGE,"E18"),sQuery(id+"F0.wireOp",EDGE,"E19")])],"isStart":false});
            cPlane(context, id + "F25", {"entities" : qUnion([Q0]), "cplaneType" : CPlaneType.OFFSET, "offset" : 20 * mm, "width" : 150 * mm, "height" : 150 * mm});
        }
        {
            var Q0;
            Q0=qCreatedBy(id+"F25.planeOp",FACE);
            var sketch = newSketch(context, id + "F26", { "sketchPlane" : qUnion([Q0])});
            skLineSegment(sketch, "E70.bottom", {"start": v(40, -57.5) * mm, "end": v(-40, -57.5) * mm, "construction": true});
            skLineSegment(sketch, "E70.top", {"start": v(40, 57.5) * mm, "end": v(-40, 57.5) * mm, "construction": true});
            skLineSegment(sketch, "E70.left", {"start": v(40, -57.5) * mm, "end": v(40, 57.5) * mm, "construction": true});
            skLineSegment(sketch, "E70.right", {"start": v(-40, -57.5) * mm, "end": v(-40, 57.5) * mm, "construction": true});
            skPoint(sketch, "E70.middle", {"position": v(0, 0) * mm});
            skCircle(sketch, "E71", {"center": v(-40, 57.5) * mm, "radius": 2.6 * mm});
            skCircle(sketch, "E72.0.1.0", {"center": v(-40, -57.5) * mm, "radius": 2.6 * mm});
            skLineSegment(sketch, "E72.direction1", {"start": v(-40, 57.5) * mm, "end": v(40, 57.5) * mm, "construction": true});
            skLineSegment(sketch, "E72.direction2", {"start": v(-40, 57.5) * mm, "end": v(-40, -57.5) * mm, "construction": true});
            skLineSegment(sketch, "E73.bottom", {"start": v(40, -62.5) * mm, "end": v(-40, -62.5) * mm});
            skLineSegment(sketch, "E73.top", {"start": v(40, 62.5) * mm, "end": v(-40, 62.5) * mm});
            skLineSegment(sketch, "E73.left", {"start": v(45, -57.5) * mm, "end": v(45, 57.5) * mm});
            skLineSegment(sketch, "E73.right", {"start": v(-45, -57.5) * mm, "end": v(-45, 57.5) * mm});
            skLineSegment(sketch, "E74", {"start": v(-13.05, 43.96) * mm, "end": v(30.5, 43.96) * mm});
            skLineSegment(sketch, "E75", {"start": v(-26.5, 21.9) * mm, "end": v(-26.5, 1.4) * mm});
            skLineSegment(sketch, "E76", {"start": v(27, 30.52) * mm, "end": v(27, 9.6) * mm});
            skLineSegment(sketch, "E77", {"start": v(-26.5, -10.7) * mm, "end": v(-26.5, -31.2) * mm});
            skLineSegment(sketch, "E78", {"start": v(27, -9.05) * mm, "end": v(27, -23.05) * mm});
            skArc(sketch, "E79.0.startCap", {"start": v(-13.05, 41.46) * mm, "mid": v(-15.55, 43.96) * mm, "end": v(-13.05, 46.46) * mm});
            skArc(sketch, "E79.0.endCap", {"start": v(30.5, 46.46) * mm, "mid": v(33, 43.96) * mm, "end": v(30.5, 41.46) * mm});
            skLineSegment(sketch, "E79.0.left", {"start": v(-13.05, 46.46) * mm, "end": v(30.5, 46.46) * mm});
            skLineSegment(sketch, "E79.0.right", {"start": v(-13.05, 41.46) * mm, "end": v(30.5, 41.46) * mm});
            skCircle(sketch, "E80", {"center": v(-20.18, 26.88) * mm, "radius": 3.75 * mm});
            skCircle(sketch, "E81", {"center": v(20.25, 4.25) * mm, "radius": 3.75 * mm});
            skCircle(sketch, "E82", {"center": v(-20.27, -4.83) * mm, "radius": 3.75 * mm});
            skCircle(sketch, "E83", {"center": v(20.32, -28.31) * mm, "radius": 3.75 * mm});
            skCircle(sketch, "E84.0.1.0", {"center": v(40, 57.5) * mm, "radius": 2.6 * mm});
            skCircle(sketch, "E84.0.1.1", {"center": v(40, -57.5) * mm, "radius": 2.6 * mm});
            skPoint(sketch, "E85.visualSharp", {"position": v(-45, 62.5) * mm});
            skArc(sketch, "E85.filletArc", {"start": v(-40, 62.5) * mm, "mid": v(-43.54, 61.04) * mm, "end": v(-45, 57.5) * mm});
            skPoint(sketch, "E86.visualSharp", {"position": v(45, 62.5) * mm});
            skArc(sketch, "E86.filletArc", {"start": v(45, 57.5) * mm, "mid": v(43.54, 61.04) * mm, "end": v(40, 62.5) * mm});
            skPoint(sketch, "E87.visualSharp", {"position": v(45, -62.5) * mm});
            skArc(sketch, "E87.filletArc", {"start": v(40, -62.5) * mm, "mid": v(43.54, -61.04) * mm, "end": v(45, -57.5) * mm});
            skPoint(sketch, "E88.visualSharp", {"position": v(-45, -62.5) * mm});
            skArc(sketch, "E88.filletArc", {"start": v(-45, -57.5) * mm, "mid": v(-43.54, -61.04) * mm, "end": v(-40, -62.5) * mm});
            skArc(sketch, "E89.0.startCap", {"start": v(-29, 21.9) * mm, "mid": v(-26.5, 24.4) * mm, "end": v(-24, 21.9) * mm});
            skArc(sketch, "E89.0.endCap", {"start": v(-24, 1.4) * mm, "mid": v(-26.5, -1.1) * mm, "end": v(-29, 1.4) * mm});
            skLineSegment(sketch, "E89.0.left", {"start": v(-24, 21.9) * mm, "end": v(-24, 1.4) * mm});
            skLineSegment(sketch, "E89.0.right", {"start": v(-29, 21.9) * mm, "end": v(-29, 1.4) * mm});
            skArc(sketch, "E89.1.startCap", {"start": v(24.5, 30.52) * mm, "mid": v(27, 33.02) * mm, "end": v(29.5, 30.52) * mm});
            skArc(sketch, "E89.1.endCap", {"start": v(29.5, 9.6) * mm, "mid": v(27, 7.1) * mm, "end": v(24.5, 9.6) * mm});
            skLineSegment(sketch, "E89.1.left", {"start": v(29.5, 30.52) * mm, "end": v(29.5, 9.6) * mm});
            skLineSegment(sketch, "E89.1.right", {"start": v(24.5, 30.52) * mm, "end": v(24.5, 9.6) * mm});
            skArc(sketch, "E89.2.startCap", {"start": v(24.5, -9.05) * mm, "mid": v(27, -6.55) * mm, "end": v(29.5, -9.05) * mm});
            skArc(sketch, "E89.2.endCap", {"start": v(29.5, -23.05) * mm, "mid": v(27, -25.55) * mm, "end": v(24.5, -23.05) * mm});
            skLineSegment(sketch, "E89.2.left", {"start": v(29.5, -9.05) * mm, "end": v(29.5, -23.05) * mm});
            skLineSegment(sketch, "E89.2.right", {"start": v(24.5, -9.05) * mm, "end": v(24.5, -23.05) * mm});
            skArc(sketch, "E89.3.startCap", {"start": v(-29, -10.7) * mm, "mid": v(-26.5, -8.2) * mm, "end": v(-24, -10.7) * mm});
            skArc(sketch, "E89.3.endCap", {"start": v(-24, -31.2) * mm, "mid": v(-26.5, -33.7) * mm, "end": v(-29, -31.2) * mm});
            skLineSegment(sketch, "E89.3.left", {"start": v(-24, -10.7) * mm, "end": v(-24, -31.2) * mm});
            skLineSegment(sketch, "E89.3.right", {"start": v(-29, -10.7) * mm, "end": v(-29, -31.2) * mm});
            skSolve(sketch);
        }
        {
            var Q0;
            Q0 = qSketchRegion(id + "F26", true);
            extrude(context, id + "F27", {"entities" : qUnion([Q0]), "depth" : 4 * mm});
        }
        {
            var Q0;
            Q0=makeQuery(id+"F27.opExtrude","CAP_FACE",FACE,{"disambiguationData":[OSD([sQuery(id+"F26.wireOp",EDGE,"E71"),sQuery(id+"F26.wireOp",EDGE,"E72.0.1.0"),sQuery(id+"F26.wireOp",EDGE,"E73.bottom"),sQuery(id+"F26.wireOp",EDGE,"E73.top"),sQuery(id+"F26.wireOp",EDGE,"E73.left"),sQuery(id+"F26.wireOp",EDGE,"E73.right"),sQuery(id+"F26.wireOp",EDGE,"E79.0.startCap"),sQuery(id+"F26.wireOp",EDGE,"E79.0.endCap"),sQuery(id+"F26.wireOp",EDGE,"E79.0.left"),sQuery(id+"F26.wireOp",EDGE,"E79.0.right"),sQuery(id+"F26.wireOp",EDGE,"E80"),sQuery(id+"F26.wireOp",EDGE,"E81"),sQuery(id+"F26.wireOp",EDGE,"E82"),sQuery(id+"F26.wireOp",EDGE,"E83"),sQuery(id+"F26.wireOp",EDGE,"E84.0.1.0"),sQuery(id+"F26.wireOp",EDGE,"E84.0.1.1"),sQuery(id+"F26.wireOp",EDGE,"E85.filletArc"),sQuery(id+"F26.wireOp",EDGE,"E86.filletArc"),sQuery(id+"F26.wireOp",EDGE,"E87.filletArc"),sQuery(id+"F26.wireOp",EDGE,"E88.filletArc"),sQuery(id+"F26.wireOp",EDGE,"E89.0.startCap"),sQuery(id+"F26.wireOp",EDGE,"E89.0.endCap"),sQuery(id+"F26.wireOp",EDGE,"E89.0.left"),sQuery(id+"F26.wireOp",EDGE,"E89.0.right"),sQuery(id+"F26.wireOp",EDGE,"E89.1.startCap"),sQuery(id+"F26.wireOp",EDGE,"E89.1.endCap"),sQuery(id+"F26.wireOp",EDGE,"E89.1.left"),sQuery(id+"F26.wireOp",EDGE,"E89.1.right"),sQuery(id+"F26.wireOp",EDGE,"E89.2.startCap"),sQuery(id+"F26.wireOp",EDGE,"E89.2.endCap"),sQuery(id+"F26.wireOp",EDGE,"E89.2.left"),sQuery(id+"F26.wireOp",EDGE,"E89.2.right"),sQuery(id+"F26.wireOp",EDGE,"E89.3.startCap"),sQuery(id+"F26.wireOp",EDGE,"E89.3.endCap"),sQuery(id+"F26.wireOp",EDGE,"E89.3.left"),sQuery(id+"F26.wireOp",EDGE,"E89.3.right")])],"isStart":false});
            var sketch = newSketch(context, id + "F28", { "sketchPlane" : qUnion([Q0])});
            skText(sketch, "E90", { "text": "OPENBUILDS", "fontName": "OpenSans-Bold.ttf"});
            skText(sketch, "E91", { "text": "MAKERSL.COM", "fontName": "OpenSans-BoldItalic.ttf"});
            const initialGuessF28  = {"E90": [-0.0375, -0.0475, 1, 0, 0.00839], "E91": [-0.0325, 0.04958, 1, 0, 0.00679]};
            skSetInitialGuess(sketch, initialGuessF28);
            skSolve(sketch);
        }
        {
            var Q0;
            Q0 = qSketchRegion(id + "F28", true);
            extrude(context, id + "F29", {"entities" : qUnion([Q0]), "operationType" : NewBodyOperationType.REMOVE, "oppositeDirection" : true, "depth" : 2 * mm});
        }
        {
            var Q0;
            {var subQ0=sQuery(id+"F26.wireOp",EDGE,"E79.0.startCap");var subQ1=sQuery(id+"F26.wireOp",EDGE,"E79.0.right");var subQ2=sQuery(id+"F26.wireOp",EDGE,"E72.0.1.0");var subQ3=sQuery(id+"F26.wireOp",EDGE,"E89.3.right");var subQ4=sQuery(id+"F26.wireOp",EDGE,"E89.3.left");var subQ5=sQuery(id+"F26.wireOp",EDGE,"E89.3.endCap");var subQ6=sQuery(id+"F26.wireOp",EDGE,"E79.0.endCap");var subQ7=sQuery(id+"F26.wireOp",EDGE,"E89.3.startCap");var subQ8=sQuery(id+"F26.wireOp",EDGE,"E89.2.right");var subQ9=sQuery(id+"F26.wireOp",EDGE,"E89.2.left");var subQ10=sQuery(id+"F26.wireOp",EDGE,"E89.2.endCap");var subQ11=sQuery(id+"F26.wireOp",EDGE,"E89.1.startCap");var subQ12=sQuery(id+"F26.wireOp",EDGE,"E73.top");var subQ13=sQuery(id+"F26.wireOp",EDGE,"E79.0.left");var subQ14=sQuery(id+"F26.wireOp",EDGE,"E87.filletArc");var subQ15=sQuery(id+"F26.wireOp",EDGE,"E88.filletArc");var subQ16=sQuery(id+"F26.wireOp",EDGE,"E89.1.left");var subQ17=sQuery(id+"F26.wireOp",EDGE,"E82");var subQ18=sQuery(id+"F26.wireOp",EDGE,"E73.bottom");var subQ19=sQuery(id+"F26.wireOp",EDGE,"E73.right");var subQ20=sQuery(id+"F26.wireOp",EDGE,"E89.2.startCap");var subQ21=sQuery(id+"F26.wireOp",EDGE,"E73.left");var subQ22=sQuery(id+"F26.wireOp",EDGE,"E86.filletArc");var subQ23=sQuery(id+"F26.wireOp",EDGE,"E89.0.left");var subQ24=sQuery(id+"F26.wireOp",EDGE,"E71");var subQ25=sQuery(id+"F26.wireOp",EDGE,"E89.0.endCap");var subQ26=sQuery(id+"F26.wireOp",EDGE,"E84.0.1.0");var subQ27=sQuery(id+"F26.wireOp",EDGE,"E85.filletArc");var subQ28=sQuery(id+"F26.wireOp",EDGE,"E84.0.1.1");var subQ29=sQuery(id+"F26.wireOp",EDGE,"E89.0.startCap");var subQ30=sQuery(id+"F26.wireOp",EDGE,"E89.1.right");var subQ31=sQuery(id+"F26.wireOp",EDGE,"E83");var subQ32=sQuery(id+"F26.wireOp",EDGE,"E89.0.right");var subQ33=sQuery(id+"F26.wireOp",EDGE,"E89.1.endCap");var subQ34=sQuery(id+"F26.wireOp",EDGE,"E81");var subQ35=sQuery(id+"F26.wireOp",EDGE,"E80");Q0=makeQuery(id+"F29.boolean.opBoolean","SPLIT",FACE,{"disambiguationData":[TD([makeQuery(id+"F27.opExtrude","SWEPT_FACE",FACE,{"disambiguationData":[OSD([subQ24])]})])],"derivedFrom":makeQuery(id+"F27.opExtrude","CAP_FACE",FACE,{"disambiguationData":[OSD([subQ24,subQ2,subQ18,subQ12,subQ21,subQ19,subQ0,subQ6,subQ13,subQ1,subQ35,subQ34,subQ17,subQ31,subQ26,subQ28,subQ27,subQ22,subQ14,subQ15,subQ29,subQ25,subQ23,subQ32,subQ11,subQ33,subQ16,subQ30,subQ20,subQ10,subQ9,subQ8,subQ7,subQ5,subQ4,subQ3])],"isStart":false})});}
            var sketch = newSketch(context, id + "F30", { "sketchPlane" : qUnion([Q0])});
            skLineSegment(sketch, "E92.bottom", {"start": v(12, -12) * mm, "end": v(-12, -12) * mm, "construction": true});
            skLineSegment(sketch, "E92.top", {"start": v(12, 12) * mm, "end": v(-12, 12) * mm, "construction": true});
            skLineSegment(sketch, "E92.left", {"start": v(12, -12) * mm, "end": v(12, 12) * mm, "construction": true});
            skLineSegment(sketch, "E92.right", {"start": v(-12, -12) * mm, "end": v(-12, 12) * mm, "construction": true});
            skPoint(sketch, "E92.middle", {"position": v(0, 0) * mm});
            skCircle(sketch, "E93", {"center": v(-12, 12) * mm, "radius": 1.1 * mm});
            skCircle(sketch, "E94.0.1.0", {"center": v(-12, -12) * mm, "radius": 1.1 * mm});
            skCircle(sketch, "E94.1.0.0", {"center": v(12, 12) * mm, "radius": 1.1 * mm});
            skCircle(sketch, "E94.1.1.0", {"center": v(12, -12) * mm, "radius": 1.1 * mm});
            skLineSegment(sketch, "E94.direction1", {"start": v(-12, 12) * mm, "end": v(12, 12) * mm, "construction": true});
            skLineSegment(sketch, "E94.direction2", {"start": v(-12, 12) * mm, "end": v(-12, -12) * mm, "construction": true});
            skCircle(sketch, "E95", {"center": v(0, 0) * mm, "radius": 14.25 * mm});
            skSolve(sketch);
        }
        {
            var Q0;
            Q0 = qSketchRegion(id + "F30", true);
            extrude(context, id + "F31", {"entities" : qUnion([Q0]), "operationType" : NewBodyOperationType.REMOVE, "oppositeDirection" : true, "depth" : 25 * mm});
        }
        {
            var Q0;
            {var subQ0=sQuery(id+"F26.wireOp",EDGE,"E79.0.startCap");var subQ1=sQuery(id+"F26.wireOp",EDGE,"E79.0.right");var subQ2=sQuery(id+"F26.wireOp",EDGE,"E72.0.1.0");var subQ3=sQuery(id+"F26.wireOp",EDGE,"E89.3.right");var subQ4=sQuery(id+"F26.wireOp",EDGE,"E89.3.left");var subQ5=sQuery(id+"F26.wireOp",EDGE,"E89.3.endCap");var subQ6=sQuery(id+"F26.wireOp",EDGE,"E79.0.endCap");var subQ7=sQuery(id+"F26.wireOp",EDGE,"E89.3.startCap");var subQ8=sQuery(id+"F26.wireOp",EDGE,"E89.2.right");var subQ9=sQuery(id+"F26.wireOp",EDGE,"E89.2.left");var subQ10=sQuery(id+"F26.wireOp",EDGE,"E89.2.endCap");var subQ11=sQuery(id+"F26.wireOp",EDGE,"E89.1.startCap");var subQ12=sQuery(id+"F26.wireOp",EDGE,"E73.top");var subQ13=sQuery(id+"F26.wireOp",EDGE,"E79.0.left");var subQ14=sQuery(id+"F26.wireOp",EDGE,"E87.filletArc");var subQ15=sQuery(id+"F26.wireOp",EDGE,"E88.filletArc");var subQ16=sQuery(id+"F26.wireOp",EDGE,"E89.1.left");var subQ17=sQuery(id+"F26.wireOp",EDGE,"E82");var subQ18=sQuery(id+"F26.wireOp",EDGE,"E73.bottom");var subQ19=sQuery(id+"F26.wireOp",EDGE,"E73.right");var subQ20=sQuery(id+"F26.wireOp",EDGE,"E89.2.startCap");var subQ21=sQuery(id+"F26.wireOp",EDGE,"E73.left");var subQ22=sQuery(id+"F26.wireOp",EDGE,"E86.filletArc");var subQ23=sQuery(id+"F26.wireOp",EDGE,"E89.0.left");var subQ24=sQuery(id+"F26.wireOp",EDGE,"E71");var subQ25=sQuery(id+"F26.wireOp",EDGE,"E89.0.endCap");var subQ26=sQuery(id+"F26.wireOp",EDGE,"E84.0.1.0");var subQ27=sQuery(id+"F26.wireOp",EDGE,"E85.filletArc");var subQ28=sQuery(id+"F26.wireOp",EDGE,"E84.0.1.1");var subQ29=sQuery(id+"F26.wireOp",EDGE,"E89.0.startCap");var subQ30=sQuery(id+"F26.wireOp",EDGE,"E89.1.right");var subQ31=sQuery(id+"F26.wireOp",EDGE,"E83");var subQ32=sQuery(id+"F26.wireOp",EDGE,"E89.0.right");var subQ33=sQuery(id+"F26.wireOp",EDGE,"E89.1.endCap");var subQ34=sQuery(id+"F26.wireOp",EDGE,"E81");var subQ35=sQuery(id+"F26.wireOp",EDGE,"E80");Q0=makeQuery(id+"F29.boolean.opBoolean","SPLIT",FACE,{"disambiguationData":[TD([makeQuery(id+"F27.opExtrude","SWEPT_FACE",FACE,{"disambiguationData":[OSD([subQ24])]})])],"derivedFrom":makeQuery(id+"F27.opExtrude","CAP_FACE",FACE,{"disambiguationData":[OSD([subQ24,subQ2,subQ18,subQ12,subQ21,subQ19,subQ0,subQ6,subQ13,subQ1,subQ35,subQ34,subQ17,subQ31,subQ26,subQ28,subQ27,subQ22,subQ14,subQ15,subQ29,subQ25,subQ23,subQ32,subQ11,subQ33,subQ16,subQ30,subQ20,subQ10,subQ9,subQ8,subQ7,subQ5,subQ4,subQ3])],"isStart":false})});}
            var sketch = newSketch(context, id + "F32", { "sketchPlane" : qUnion([Q0])});
            skText(sketch, "E96", { "text": "Y-AXIS", "fontName": "OpenSans-Bold.ttf"});
            skText(sketch, "E97", { "text": "Z-AXIS", "fontName": "OpenSans-Bold.ttf"});
            skText(sketch, "E98", { "text": "CLONE", "fontName": "OpenSans-Bold.ttf"});
            skText(sketch, "E99", { "text": "X-AXIS", "fontName": "OpenSans-Bold.ttf"});
            const initialGuessF32  = {"E96": [-0.01361, 0.0241, 1, 0, 0.006], "E97": [0.02524, 0.00095, 1, 0, 0.00501], "E98": [0.02535, -0.03206, 1, 0, 0.00523], "E99": [-0.02127, -0.0229, 1, 0, 0.00643]};
            skSetInitialGuess(sketch, initialGuessF32);
            skSolve(sketch);
        }
        {
            var Q0;
            Q0=makeQuery(id+"F27.opExtrude","SWEPT_BODY",BODY,{"disambiguationData":[OSD([sQuery(id+"F26.wireOp",EDGE,"E71"),sQuery(id+"F26.wireOp",EDGE,"E72.0.1.0"),sQuery(id+"F26.wireOp",EDGE,"E73.bottom"),sQuery(id+"F26.wireOp",EDGE,"E73.top"),sQuery(id+"F26.wireOp",EDGE,"E73.left"),sQuery(id+"F26.wireOp",EDGE,"E73.right"),sQuery(id+"F26.wireOp",EDGE,"E79.0.startCap"),sQuery(id+"F26.wireOp",EDGE,"E79.0.endCap"),sQuery(id+"F26.wireOp",EDGE,"E79.0.left"),sQuery(id+"F26.wireOp",EDGE,"E79.0.right"),sQuery(id+"F26.wireOp",EDGE,"E80"),sQuery(id+"F26.wireOp",EDGE,"E81"),sQuery(id+"F26.wireOp",EDGE,"E82"),sQuery(id+"F26.wireOp",EDGE,"E83"),sQuery(id+"F26.wireOp",EDGE,"E84.0.1.0"),sQuery(id+"F26.wireOp",EDGE,"E84.0.1.1"),sQuery(id+"F26.wireOp",EDGE,"E85.filletArc"),sQuery(id+"F26.wireOp",EDGE,"E86.filletArc"),sQuery(id+"F26.wireOp",EDGE,"E87.filletArc"),sQuery(id+"F26.wireOp",EDGE,"E88.filletArc"),sQuery(id+"F26.wireOp",EDGE,"E89.0.startCap"),sQuery(id+"F26.wireOp",EDGE,"E89.0.endCap"),sQuery(id+"F26.wireOp",EDGE,"E89.0.left"),sQuery(id+"F26.wireOp",EDGE,"E89.0.right"),sQuery(id+"F26.wireOp",EDGE,"E89.1.startCap"),sQuery(id+"F26.wireOp",EDGE,"E89.1.endCap"),sQuery(id+"F26.wireOp",EDGE,"E89.1.left"),sQuery(id+"F26.wireOp",EDGE,"E89.1.right"),sQuery(id+"F26.wireOp",EDGE,"E89.2.startCap"),sQuery(id+"F26.wireOp",EDGE,"E89.2.endCap"),sQuery(id+"F26.wireOp",EDGE,"E89.2.left"),sQuery(id+"F26.wireOp",EDGE,"E89.2.right"),sQuery(id+"F26.wireOp",EDGE,"E89.3.startCap"),sQuery(id+"F26.wireOp",EDGE,"E89.3.endCap"),sQuery(id+"F26.wireOp",EDGE,"E89.3.left"),sQuery(id+"F26.wireOp",EDGE,"E89.3.right")])]});
            transform(context, id + "F33", {"entities" : qUnion([Q0]), "transformType" : TransformType.TRANSLATION_3D, "dx" : 0 * mm, "dy" : 0 * mm, "dz" : 0 * mm, "makeCopy" : true});
        }
        {
            var Q0;
            Q0=makeQuery(id+"F32.imprint","IMPRINT",FACE,{"disambiguationData":[TD([[makeQuery(id+"F32.imprint","IMPRINT",EDGE,{"derivedFrom":sQuery(id+"F32.wireOp",EDGE,"E96.sketch_text.stroke-0")}),1.0]])]});
            var sketch = newSketch(context, id + "F34", { "sketchPlane" : qUnion([Q0])});
            skLineSegment(sketch, "E100.0", {"start": v(40, 62.5) * mm, "end": v(-40, 62.5) * mm});
            skPoint(sketch, "E101.0", {"position": v(43.54, 61.04) * mm});
            skLineSegment(sketch, "E102.0", {"start": v(45, -57.5) * mm, "end": v(45, 57.5) * mm});
            skPoint(sketch, "E103.0", {"position": v(43.54, -61.04) * mm});
            skLineSegment(sketch, "E104.0", {"start": v(40, -62.5) * mm, "end": v(-40, -62.5) * mm});
            skPoint(sketch, "E105.0", {"position": v(-43.54, -61.04) * mm});
            skLineSegment(sketch, "E106.0", {"start": v(-45, -57.5) * mm, "end": v(-45, 57.5) * mm});
            skPoint(sketch, "E107.0", {"position": v(-43.54, 61.04) * mm});
            skCircle(sketch, "E108.0", {"center": v(-40, 57.5) * mm, "radius": 2.6 * mm});
            skCircle(sketch, "E109.0", {"center": v(40, 57.5) * mm, "radius": 2.6 * mm});
            skCircle(sketch, "E110.0", {"center": v(40, -57.5) * mm, "radius": 2.6 * mm});
            skCircle(sketch, "E111.0", {"center": v(-40, -57.5) * mm, "radius": 2.6 * mm});
            skArc(sketch, "E112.0", {"start": v(-40, 62.5) * mm, "mid": v(-43.54, 61.04) * mm, "end": v(-45, 57.5) * mm});
            skArc(sketch, "E113.0", {"start": v(45, 57.5) * mm, "mid": v(43.54, 61.04) * mm, "end": v(40, 62.5) * mm});
            skArc(sketch, "E114.0", {"start": v(40, -62.5) * mm, "mid": v(43.54, -61.04) * mm, "end": v(45, -57.5) * mm});
            skPoint(sketch, "E115.newPointA", {"position": v(-45, -57.5) * mm});
            skPoint(sketch, "E115.newPointB", {"position": v(-40, -62.5) * mm});
            skArc(sketch, "E115.filletArc", {"start": v(-45, -57.5) * mm, "mid": v(-43.54, -61.04) * mm, "end": v(-40, -62.5) * mm});
            skLineSegment(sketch, "E116", {"start": v(0, 62.5) * mm, "end": v(0, -62.5) * mm, "construction": true});
            skCircle(sketch, "E117", {"center": v(0, 21) * mm, "radius": 19 * mm});
            skCircle(sketch, "E118", {"center": v(0, -21) * mm, "radius": 19 * mm});
            skLineSegment(sketch, "E119.bottom", {"start": v(20, 1) * mm, "end": v(-20, 1) * mm, "construction": true});
            skLineSegment(sketch, "E119.top", {"start": v(20, 41) * mm, "end": v(-20, 41) * mm, "construction": true});
            skLineSegment(sketch, "E119.left", {"start": v(20, 1) * mm, "end": v(20, 41) * mm, "construction": true});
            skLineSegment(sketch, "E119.right", {"start": v(-20, 1) * mm, "end": v(-20, 41) * mm, "construction": true});
            skLineSegment(sketch, "E120.bottom", {"start": v(20, -41) * mm, "end": v(-20, -41) * mm, "construction": true});
            skLineSegment(sketch, "E120.top", {"start": v(20, -1) * mm, "end": v(-20, -1) * mm, "construction": true});
            skLineSegment(sketch, "E120.left", {"start": v(20, -41) * mm, "end": v(20, -1) * mm, "construction": true});
            skLineSegment(sketch, "E120.right", {"start": v(-20, -41) * mm, "end": v(-20, -1) * mm, "construction": true});
            skLineSegment(sketch, "E121.bottom", {"start": v(16, -37) * mm, "end": v(-16, -37) * mm, "construction": true});
            skLineSegment(sketch, "E121.top", {"start": v(16, -5) * mm, "end": v(-16, -5) * mm, "construction": true});
            skLineSegment(sketch, "E121.left", {"start": v(16, -37) * mm, "end": v(16, -5) * mm, "construction": true});
            skLineSegment(sketch, "E121.right", {"start": v(-16, -37) * mm, "end": v(-16, -5) * mm, "construction": true});
            skLineSegment(sketch, "E122.bottom", {"start": v(16, 5) * mm, "end": v(-16, 5) * mm, "construction": true});
            skLineSegment(sketch, "E122.top", {"start": v(16, 37) * mm, "end": v(-16, 37) * mm, "construction": true});
            skLineSegment(sketch, "E122.left", {"start": v(16, 5) * mm, "end": v(16, 37) * mm, "construction": true});
            skLineSegment(sketch, "E122.right", {"start": v(-16, 5) * mm, "end": v(-16, 37) * mm, "construction": true});
            skCircle(sketch, "E123", {"center": v(-16, 37) * mm, "radius": 1.1 * mm});
            skCircle(sketch, "E124", {"center": v(-16, -5) * mm, "radius": 1.1 * mm});
            skCircle(sketch, "E125.0.1.0", {"center": v(-16, 5) * mm, "radius": 1.1 * mm});
            skCircle(sketch, "E125.1.0.0", {"center": v(16, 37) * mm, "radius": 1.1 * mm});
            skCircle(sketch, "E125.1.1.0", {"center": v(16, 5) * mm, "radius": 1.1 * mm});
            skLineSegment(sketch, "E125.direction1", {"start": v(-16, 37) * mm, "end": v(16, 37) * mm, "construction": true});
            skLineSegment(sketch, "E125.direction2", {"start": v(-16, 37) * mm, "end": v(-16, 5) * mm, "construction": true});
            skCircle(sketch, "E126.0.1.0", {"center": v(-16, -37) * mm, "radius": 1.1 * mm});
            skCircle(sketch, "E126.1.0.0", {"center": v(16, -5) * mm, "radius": 1.1 * mm});
            skCircle(sketch, "E126.1.1.0", {"center": v(16, -37) * mm, "radius": 1.1 * mm});
            skLineSegment(sketch, "E126.direction1", {"start": v(-16, -5) * mm, "end": v(16, -5) * mm, "construction": true});
            skLineSegment(sketch, "E126.direction2", {"start": v(-16, -5) * mm, "end": v(-16, -37) * mm, "construction": true});
            skSolve(sketch);
        }
        {
            var Q0;
            Q0 = qSketchRegion(id + "F34", true);
            extrude(context, id + "F35", {"entities" : qUnion([Q0]), "depth" : 4 * mm});
        }
    });
